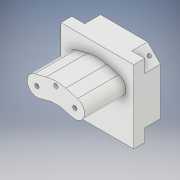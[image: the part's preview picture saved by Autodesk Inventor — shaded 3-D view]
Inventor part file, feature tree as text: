
AUTODESK INVENTOR PART (.ipt)
format: ipt  version: 2017 SP1 (Build 210196100, 196)  size: 181,248 bytes
history: native  units: in
note: dims shown in document units (in); Inventor stores cm internally (conversion verified against a paired STEP export)
features: extrude x6, sketch x6, projected_geometry x1
ambient origin geometry x8: Origin, YZ Plane, XZ Plane, XY Plane, X Axis, Y Axis, Z Axis, Center Point
bodies: Solid1 (feature_tree)
feature tree (13):
  extrude  "Extrusion1"  Depth=2.3622in
  extrude  "Extrusion2"  Depth=0.8661in
  extrude  "Extrusion7"  Depth=0.5906in
  extrude  "Extrusion8"  Depth=0.5118in TaperAngle=0.0deg
  extrude  "Extrusion9"  Depth=0.6299in
  extrude  "Extrusion10"  Depth=0.3937in
  sketch  "Sketch1"  dims[d0=2.3622in d1=2.3622in]
  sketch  "Sketch2"  dims[d2=0.8661in d3=0.0in d4=0.5906in]
  sketch  "Sketch7"  dims[d7=0.5906in d8=0.5906in]
  sketch  "Sketch8"  dims[d9=0.5906in d10=0.5118in d11=0.0in]
  sketch  "Sketch9"  dims[d28=0.6299in d29=0.6299in]
  sketch  "Sketch10"  dims[d30=0.6299in d31=0.3937in d32=0.3937in d33=0.6299in d34=0.6299in d36=75.0deg d37=0.8268in d38=1.3386in d39=0.0in d40=0.1181in d41=0.1575in d42=1.3386in d43=0.0in d44=0.1181in d45=0.1575in d46=1.3386in d47=0.0in d48=0.1378in d49=0.1378in d50=0.1378in d51=0.5118in d52=1.1417in d53=0.0in]
  projected_geometry  "Projected Loop1"
